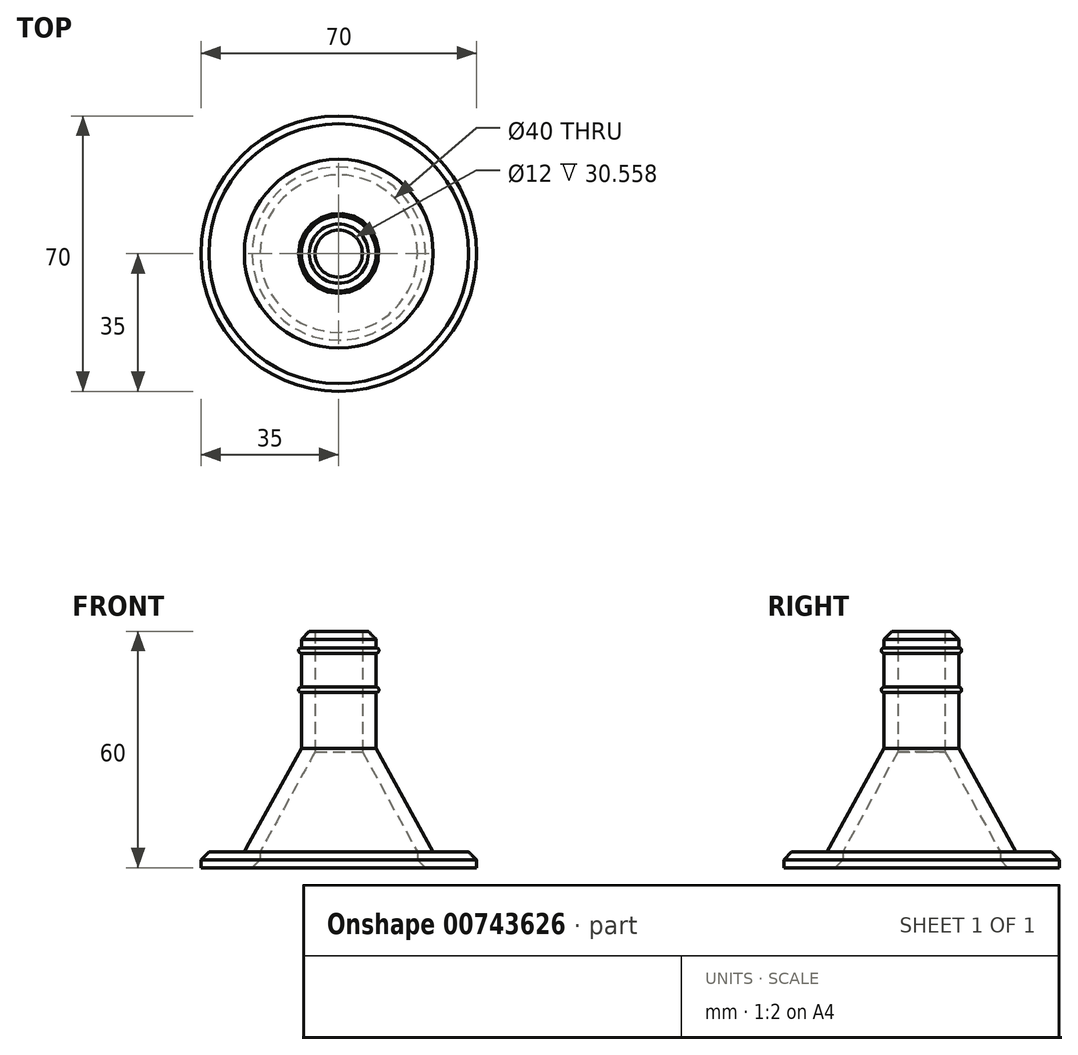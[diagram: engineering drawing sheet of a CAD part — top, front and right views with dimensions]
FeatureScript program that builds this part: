
annotation { "Feature Type Name" : "Feature", "Feature Type Description" : "" }
export const myFeature = defineFeature(function(context is Context, id is Id, definition is map)
    precondition{}
    {
        {
            var Q0;
            Q0=qCreatedBy(makeId("Front.planeOp"),FACE);
            var sketch = newSketch(context, id + "F0", { "sketchPlane" : qUnion([Q0])});
            skLineSegment(sketch, "E0", {"start": v(-35, 0) * mm, "end": v(-35, 4) * mm});
            skLineSegment(sketch, "E1", {"start": v(-35, 4) * mm, "end": v(-24, 4) * mm});
            skLineSegment(sketch, "E2", {"start": v(-24, 4) * mm, "end": v(-9.5, 30.34) * mm});
            skLineSegment(sketch, "E3", {"start": v(-9.5, 30.34) * mm, "end": v(-9.5, 60) * mm});
            skLineSegment(sketch, "E4", {"start": v(-9.5, 60) * mm, "end": v(-6, 60) * mm});
            skLineSegment(sketch, "E5", {"start": v(-6, 60) * mm, "end": v(-6, 29.44) * mm});
            skLineSegment(sketch, "E6", {"start": v(-6, 29.44) * mm, "end": v(-20, 4) * mm});
            skLineSegment(sketch, "E7", {"start": v(-20, 4) * mm, "end": v(-20, 0) * mm});
            skLineSegment(sketch, "E8", {"start": v(-20, 0) * mm, "end": v(-35, 0) * mm});
            skCircle(sketch, "E9", {"center": v(-9.5, 55.17) * mm, "radius": 0.7 * mm});
            skCircle(sketch, "E10", {"center": v(-9.5, 45.17) * mm, "radius": 0.7 * mm});
            skLineSegment(sketch, "E11", {"start": v(0, -49.54) * mm, "end": v(0, 94.53) * mm, "construction": true});
            skSolve(sketch);
        }
        {
            var Q0;
            Q0 = qSketchRegion(id + "F0", true);
            var Q1;
            Q1=sQuery(id+"F0.wireOp",EDGE,"E11");
            revolve(context, id + "F1", {"surfaceOperationType" : NewSurfaceOperationType.NEW, "entities" : qUnion([Q0]), "axis" : qUnion([Q1]), "revolveType" : RevolveType.FULL});
        }
        {
            var Q0;
            Q0=makeQuery(id+"F1.opRevolve","SWEPT_EDGE",EDGE,{"disambiguationData":[OSD([sQuery(id+"F0.wireOp",EDGE,"E0"),sQuery(id+"F0.wireOp",EDGE,"E1")])]});
            var Q1;
            Q1=makeQuery(id+"F1.opRevolve","SWEPT_EDGE",EDGE,{"disambiguationData":[OSD([sQuery(id+"F0.wireOp",EDGE,"E3"),sQuery(id+"F0.wireOp",EDGE,"E4")])]});
            var Q2;
            Q2=makeQuery(id+"F1.opRevolve","SWEPT_EDGE",EDGE,{"disambiguationData":[OSD([sQuery(id+"F0.wireOp",EDGE,"E7"),sQuery(id+"F0.wireOp",EDGE,"E8")])]});
            chamfer(context, id + "F2", {"entities" : qUnion([Q0, Q1, Q2]), "width" : 2 * mm, "tangentPropagation" : true});
        }
    });
